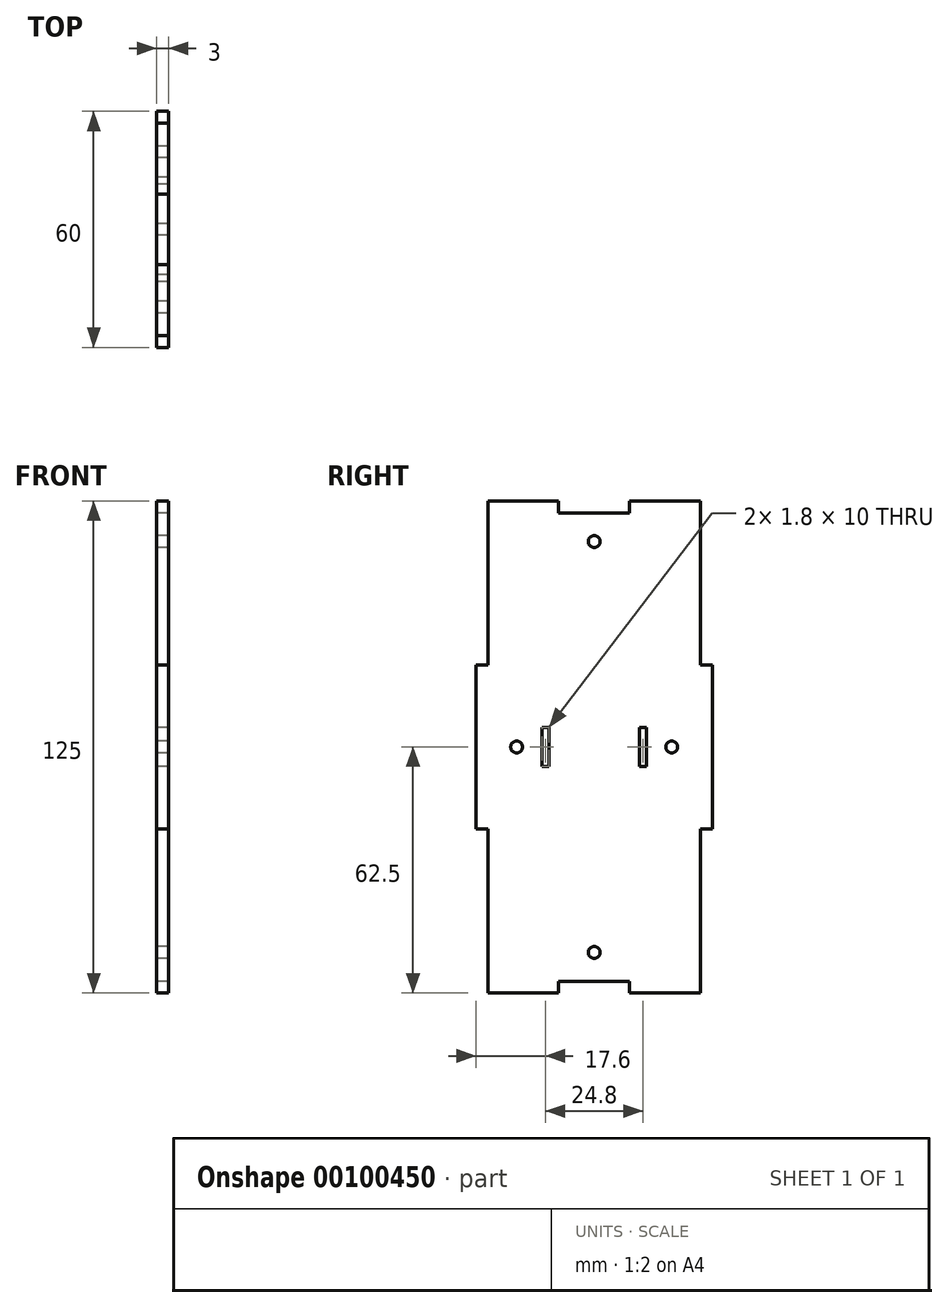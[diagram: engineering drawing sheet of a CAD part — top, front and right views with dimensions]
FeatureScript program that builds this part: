
annotation { "Feature Type Name" : "Feature", "Feature Type Description" : "" }
export const myFeature = defineFeature(function(context is Context, id is Id, definition is map)
    precondition{}
    {
        {
            var Q0;
            Q0=qCreatedBy(makeId("Right.planeOp"),FACE);
            var sketch = newSketch(context, id + "F0", { "sketchPlane" : qUnion([Q0])});
            skLineSegment(sketch, "E0.left", {"start": v(-30, 20.83) * mm, "end": v(-30, -20.83) * mm});
            skLineSegment(sketch, "E1.bottom", {"start": v(-30, 20.83) * mm, "end": v(-27, 20.83) * mm});
            skLineSegment(sketch, "E1.right", {"start": v(-27, 20.83) * mm, "end": v(-27, 62.5) * mm});
            skLineSegment(sketch, "E2.bottom", {"start": v(-30, -20.83) * mm, "end": v(-27, -20.83) * mm});
            skLineSegment(sketch, "E2.right", {"start": v(-27, -20.83) * mm, "end": v(-27, -62.5) * mm});
            skLineSegment(sketch, "E3.left", {"start": v(-9, 62.5) * mm, "end": v(-9, 59.5) * mm});
            skLineSegment(sketch, "E4.left", {"start": v(-9, -62.5) * mm, "end": v(-9, -59.5) * mm});
            skLineSegment(sketch, "E5", {"start": v(-9, 59.5) * mm, "end": v(0, 59.5) * mm});
            skLineSegment(sketch, "E6", {"start": v(0, 59.5) * mm, "end": v(0, 53.7) * mm});
            skLineSegment(sketch, "E7", {"start": v(0, -59.5) * mm, "end": v(-9, -59.5) * mm});
            skLineSegment(sketch, "E8", {"start": v(-27, 62.5) * mm, "end": v(-18, 62.5) * mm});
            skLineSegment(sketch, "E9", {"start": v(-18, 62.5) * mm, "end": v(-9, 62.5) * mm});
            skLineSegment(sketch, "E10", {"start": v(-9, -62.5) * mm, "end": v(-18, -62.5) * mm});
            skLineSegment(sketch, "E11", {"start": v(-18, -62.5) * mm, "end": v(-27, -62.5) * mm});
            skCircle(sketch, "E12", {"center": v(-19.7, 0) * mm, "radius": 1.5 * mm});
            skLineSegment(sketch, "E13.bottom", {"start": v(-13.3, 5) * mm, "end": v(-11.5, 5) * mm});
            skLineSegment(sketch, "E13.top", {"start": v(-13.3, -5) * mm, "end": v(-11.5, -5) * mm});
            skLineSegment(sketch, "E13.left", {"start": v(-13.3, 5) * mm, "end": v(-13.3, -5) * mm});
            skLineSegment(sketch, "E13.right", {"start": v(-11.5, 5) * mm, "end": v(-11.5, -5) * mm});
            skArc(sketch, "E14", {"start": v(0, 53.7) * mm, "mid": v(-1.5, 52.2) * mm, "end": v(0, 50.7) * mm});
            skArc(sketch, "E15.MirrorCS", {"start": v(0, -53.7) * mm, "mid": v(-1.5, -52.2) * mm, "end": v(0, -50.7) * mm});
            skLineSegment(sketch, "E16.trimOffspring", {"start": v(0, 50.7) * mm, "end": v(0, -50.7) * mm});
            skLineSegment(sketch, "E17.trimOffspring", {"start": v(0, -53.7) * mm, "end": v(0, -59.5) * mm});
            skArc(sketch, "E18.MirrorCS", {"start": v(0, 53.7) * mm, "mid": v(1.5, 52.2) * mm, "end": v(0, 50.7) * mm});
            skLineSegment(sketch, "E19.MirrorCS", {"start": v(13.3, 5) * mm, "end": v(11.5, 5) * mm});
            skArc(sketch, "E20.MirrorCS", {"start": v(0, -53.7) * mm, "mid": v(1.5, -52.2) * mm, "end": v(0, -50.7) * mm});
            skLineSegment(sketch, "E21.MirrorCS", {"start": v(30, 20.83) * mm, "end": v(27, 20.83) * mm});
            skLineSegment(sketch, "E22.MirrorCS", {"start": v(9, -62.5) * mm, "end": v(9, -59.5) * mm});
            skLineSegment(sketch, "E23.MirrorCS", {"start": v(9, -62.5) * mm, "end": v(18, -62.5) * mm});
            skLineSegment(sketch, "E24.MirrorCS", {"start": v(30, -20.83) * mm, "end": v(27, -20.83) * mm});
            skLineSegment(sketch, "E25.MirrorCS", {"start": v(13.3, -5) * mm, "end": v(11.5, -5) * mm});
            skLineSegment(sketch, "E26.MirrorCS", {"start": v(18, 62.5) * mm, "end": v(9, 62.5) * mm});
            skLineSegment(sketch, "E27.MirrorCS", {"start": v(9, 62.5) * mm, "end": v(9, 59.5) * mm});
            skLineSegment(sketch, "E28.MirrorCS", {"start": v(11.5, 5) * mm, "end": v(11.5, -5) * mm});
            skLineSegment(sketch, "E29.MirrorCS", {"start": v(9, 59.5) * mm, "end": v(0, 59.5) * mm});
            skCircle(sketch, "E30.MirrorC", {"center": v(19.7, 0) * mm, "radius": 1.5 * mm});
            skLineSegment(sketch, "E31.MirrorCS", {"start": v(30, 20.83) * mm, "end": v(30, -20.83) * mm});
            skLineSegment(sketch, "E32.MirrorCS", {"start": v(27, -20.83) * mm, "end": v(27, -62.5) * mm});
            skLineSegment(sketch, "E33.MirrorCS", {"start": v(13.3, 5) * mm, "end": v(13.3, -5) * mm});
            skLineSegment(sketch, "E34.MirrorCS", {"start": v(0, -59.5) * mm, "end": v(9, -59.5) * mm});
            skLineSegment(sketch, "E35.MirrorCS", {"start": v(27, 62.5) * mm, "end": v(18, 62.5) * mm});
            skLineSegment(sketch, "E36.MirrorCS", {"start": v(27, 20.83) * mm, "end": v(27, 62.5) * mm});
            skLineSegment(sketch, "E37.MirrorCS", {"start": v(18, -62.5) * mm, "end": v(27, -62.5) * mm});
            skSolve(sketch);
        }
        {
            var Q0;
            Q0=qSketchRegion(id+"F0",true);
            extrude(context, id + "F1", {"entities" : qUnion([Q0]), "depth" : 3 * mm});
        }
    });
